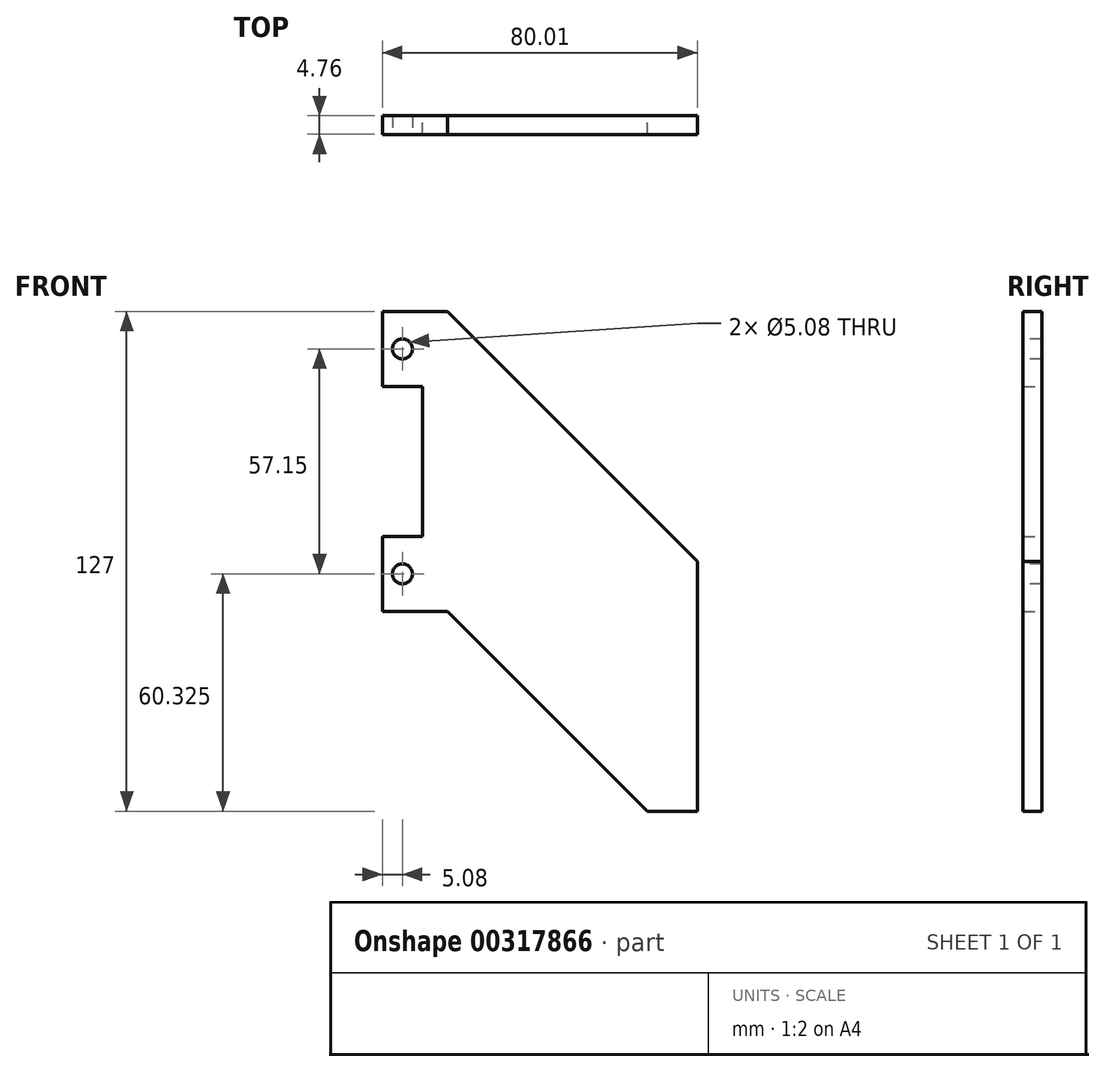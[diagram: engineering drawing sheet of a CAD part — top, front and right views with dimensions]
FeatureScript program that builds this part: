
annotation { "Feature Type Name" : "Feature", "Feature Type Description" : "" }
export const myFeature = defineFeature(function(context is Context, id is Id, definition is map)
    precondition{}
    {
        {
            var Q0;
            Q0=qCreatedBy(makeId("Front.planeOp"),FACE);
            var sketch = newSketch(context, id + "F0", { "sketchPlane" : qUnion([Q0])});
            skLineSegment(sketch, "E0", {"start": v(0, 76.2) * mm, "end": v(63.5, 12.7) * mm});
            skLineSegment(sketch, "E1", {"start": v(63.5, 12.7) * mm, "end": v(63.5, -50.8) * mm});
            skLineSegment(sketch, "E2", {"start": v(63.5, -50.8) * mm, "end": v(50.8, -50.8) * mm});
            skLineSegment(sketch, "E3", {"start": v(50.8, -50.8) * mm, "end": v(0, 0) * mm});
            skArc(sketch, "E4", {"start": v(63.5, -50.8) * mm, "mid": v(46.74, 20.2) * mm, "end": v(0, 76.2) * mm, "construction": true});
            skArc(sketch, "E5", {"start": v(63.5, -50.8) * mm, "mid": v(33.2, -23.58) * mm, "end": v(0, 0) * mm, "construction": true});
            skLineSegment(sketch, "E6.bottom", {"start": v(0, 76.2) * mm, "end": v(-6.35, 76.2) * mm});
            skLineSegment(sketch, "E6.top", {"start": v(0, 0) * mm, "end": v(-6.35, 0) * mm});
            skLineSegment(sketch, "E6.right", {"start": v(-6.35, 76.2) * mm, "end": v(-6.35, 0) * mm, "construction": true});
            skLineSegment(sketch, "E7.bottom", {"start": v(0, 76.2) * mm, "end": v(-16.51, 76.2) * mm});
            skLineSegment(sketch, "E7.top", {"start": v(-6.35, 57.15) * mm, "end": v(-16.51, 57.15) * mm});
            skLineSegment(sketch, "E7.right", {"start": v(-16.51, 76.2) * mm, "end": v(-16.51, 57.15) * mm});
            skLineSegment(sketch, "E8.bottom", {"start": v(0, 0) * mm, "end": v(-16.5, 0) * mm});
            skLineSegment(sketch, "E8.top", {"start": v(-6.35, 19.05) * mm, "end": v(-16.5, 19.05) * mm});
            skLineSegment(sketch, "E8.right", {"start": v(-16.5, 0) * mm, "end": v(-16.5, 19.05) * mm});
            skLineSegment(sketch, "E9.bottom", {"start": v(-6.35, 28.57) * mm, "end": v(-16.5, 28.57) * mm, "construction": true});
            skLineSegment(sketch, "E9.top", {"start": v(-6.35, 47.62) * mm, "end": v(-16.5, 47.62) * mm, "construction": true});
            skLineSegment(sketch, "E9.right", {"start": v(-16.5, 28.57) * mm, "end": v(-16.5, 47.62) * mm, "construction": true});
            skLineSegment(sketch, "E10", {"start": v(-6.35, 57.15) * mm, "end": v(-6.35, 47.62) * mm});
            skLineSegment(sketch, "E11", {"start": v(-6.35, 28.57) * mm, "end": v(-6.35, 19.05) * mm});
            skLineSegment(sketch, "E12", {"start": v(0, 76.2) * mm, "end": v(0, 0) * mm, "construction": true});
            skLineSegment(sketch, "E13", {"start": v(-6.35, 47.62) * mm, "end": v(-6.35, 28.57) * mm});
            skSolve(sketch);
        }
        {
            var Q0;
            {var subQ5=sQuery(id+"F0.wireOp",EDGE,"E0");Q0=makeQuery(id+"F0.imprint","IMPRINT",FACE,{"disambiguationData":[TD([[makeQuery(id+"F0.imprint","IMPRINT",EDGE,{"derivedFrom":subQ5}),-1.0]])]});}
            extrude(context, id + "F1", {"entities" : qUnion([Q0]), "endBound" : BoundingType.SYMMETRIC, "depth" : 4.76 * mm});
        }
        {
            var Q0;
            Q0=makeQuery(id+"F1.opExtrude","CAP_FACE",FACE,{"disambiguationData":[OSD([sQuery(id+"F0.wireOp",EDGE,"E4"),sQuery(id+"F0.wireOp",EDGE,"E5"),sQuery(id+"F0.wireOp",EDGE,"E7.bottom"),sQuery(id+"F0.wireOp",EDGE,"E7.top"),sQuery(id+"F0.wireOp",EDGE,"E7.right"),sQuery(id+"F0.wireOp",EDGE,"E8.bottom"),sQuery(id+"F0.wireOp",EDGE,"E8.top"),sQuery(id+"F0.wireOp",EDGE,"E8.right"),sQuery(id+"F0.wireOp",EDGE,"E9.bottom"),sQuery(id+"F0.wireOp",EDGE,"E9.top"),sQuery(id+"F0.wireOp",EDGE,"E9.right"),sQuery(id+"F0.wireOp",EDGE,"E10"),sQuery(id+"F0.wireOp",EDGE,"E11")])],"isStart":false});
            var sketch = newSketch(context, id + "F2", { "sketchPlane" : qUnion([Q0])});
            skLineSegment(sketch, "E14", {"start": v(-11.43, 66.67) * mm, "end": v(-11.43, 9.53) * mm, "construction": true});
            skPoint(sketch, "E14.startSnap0", {"position": v(-16.51, 66.67) * mm});
            skPoint(sketch, "E14.endSnap0", {"position": v(-16.5, 9.53) * mm});
            skPoint(sketch, "E15", {"position": v(-11.43, 38.1) * mm});
            skSolve(sketch);
        }
        {
            var Q0;
            Q0=sQuery(id+"F2.wireOp",VERTEX,"E14.start");
            var Q1;
            Q1=sQuery(id+"F2.wireOp",VERTEX,"E15");
            var Q2;
            Q2=sQuery(id+"F2.wireOp",VERTEX,"E14.end");
            var Q3;
            Q3=makeQuery(id+"F1.opExtrude","SWEPT_BODY",BODY,{"disambiguationData":[OSD([sQuery(id+"F0.wireOp",EDGE,"E4"),sQuery(id+"F0.wireOp",EDGE,"E5"),sQuery(id+"F0.wireOp",EDGE,"E7.bottom"),sQuery(id+"F0.wireOp",EDGE,"E7.top"),sQuery(id+"F0.wireOp",EDGE,"E7.right"),sQuery(id+"F0.wireOp",EDGE,"E8.bottom"),sQuery(id+"F0.wireOp",EDGE,"E8.top"),sQuery(id+"F0.wireOp",EDGE,"E8.right"),sQuery(id+"F0.wireOp",EDGE,"E9.bottom"),sQuery(id+"F0.wireOp",EDGE,"E9.top"),sQuery(id+"F0.wireOp",EDGE,"E9.right"),sQuery(id+"F0.wireOp",EDGE,"E10"),sQuery(id+"F0.wireOp",EDGE,"E11")])]});
            hole(context, id + "F3", {"style" : HoleStyle.SIMPLE, "endStyle" : HoleEndStyle.THROUGH, "holeDiameter" : 5.08 * mm, "tappedDepth" : 12.7 * mm, "tapClearance" : 3, "locations" : qUnion([Q0, Q1, Q2]), "scope" : qUnion([Q3])});
        }
    });
